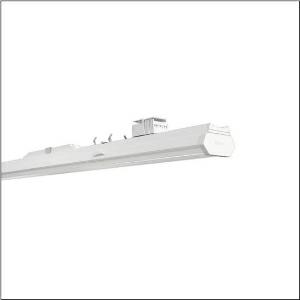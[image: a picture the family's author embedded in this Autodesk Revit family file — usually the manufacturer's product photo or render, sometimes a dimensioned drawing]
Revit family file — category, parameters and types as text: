
# Revit family: licross_r__11_protected_mo_51td1bdn49xg_f089
name_source: partatom
category: Lighting Fixtures
units: mm (PartAtom-declared; Revit-internal decimal feet)

## family parameters
Cut with Voids When Loaded = No
Host = Face
Light Source = No
Part Type = Normal
Room Calculation Point = No
Round Connector Dimension = Use Diameter
Shared = No

## types (1)
- --- (1 x LED, 9370 lm, 57.1 W, 4000K)
    Apparent Load = 57 VA
    CIE Flux Codes = 54 82 95 97 100
    Color Rendering = 80
    Color Temperature = 4000K
    Default Elevation = 1800 mm
    Description = Licross® 11 Protected MO, luminaire insert, of sheet steel, galvanised, coil coated, white, length: 1.500mm, width: 90mm, height: 101mm, LED rated luminous flux: 9.370lm, light colour: 840, control gear: DALI 2, with plug, 5-pole, with phase selection, mains connection: 220..240V, AC, 50/60Hz, rated input power: 57W, internal wiring halogen-free, primary optical cover: cover, of PMMA, light emission: direct distribution, primary light characteristic: symmetric, protection rating (complete): IP54, insulation class (complete): insulation class I (protective earthing), certification: CE, ENEC, VDE, UKCA, protection symbol: D if used in an environment with non-conductive dust loads with corresponding accessories, impact resistance: IK06, permissible ambient temperature for indoor applications: -25..+35°C, corresponds to IFS (International Featured Standards) requirements for safety and quality in the food industry, reducing of maximum allowable ambient temperature of 5°C with ceiling mounting, LABS conformity tested according to VDMA 24364:2018-05, packaging unit: 1 piece
    Height = 92 mm
    Lamp = 1 x LED
    Lamp Light Flux = 9370 lm
    Lamp Power = 57.1 W
    Lamp count = 1
    Length = 1500 mm
    Luminous efficacy = 164 lm/W
    Manufacturer = Siteco
    ModVariant = No
    Model = 51TD1BDN49XG
    Mounting Place = Ceiling
    Mounting Type = Pendant
    Number of Poles = 1
    OnlyDefault = Yes
    Power Factor = 1
    Product Name = Licross® 11 Protected MO
    Product group = luminaire insert | ceiling pendant
    ProductGroupID = 902
    Protection Class = Protection class I
    Protection Degree = IP 54
    RLX_Detail_Level = 1
    RLX_Emergency_Light_Flux = 0 lm
    RLX_Emergency_Type = 0
    RLX_Emergency_Type_DB = No
    RlxData = <blob elided: 24329 chars, md5=d1ffd6a9>
    Socket = socket
    Standby Power = 0 W
    System Light Flux = 9370 lm
    System Power = 57 W
    Type Comments = factory setting: luminous flux: 100 % | dim-lin: 254 | 378 mA
    Type Image = l_1256145.jpg
    URL = http://relux.com
    VarID = @adj_122659
    Voltage = 0 V
    Weight = 0.00 kg
    Width = 88 mm

## geometry (parser evidence)
native form markers: Blend x4, Sweep x10
no freeform markers — native parametric forms only
